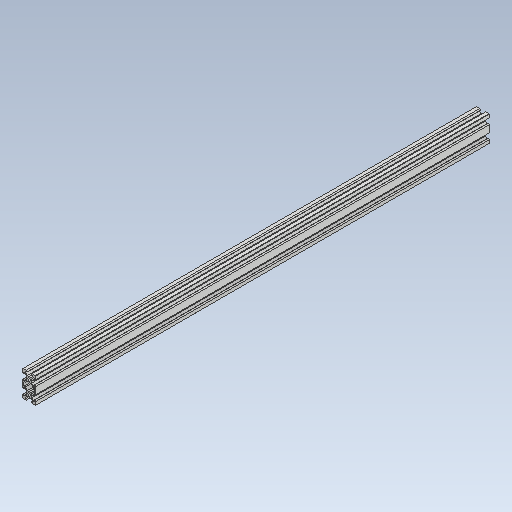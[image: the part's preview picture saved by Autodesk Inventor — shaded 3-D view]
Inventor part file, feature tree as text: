
AUTODESK INVENTOR PART (.ipt)
format: ipt  version: 2020 (Build 240168000, 168)  size: 220,160 bytes
history: native  units: mm
features: extrude x1, sketch x1
ambient origin geometry x8: Origin, YZ Plane, XZ Plane, XY Plane, X Axis, Y Axis, Z Axis, Center Point
bodies: Solid1 (feature_tree)
feature tree (2):
  extrude  "Extrusion1"  [1 undecoded]
  sketch  "Sketch1"  dims[d0=700.0mm d1=0.0mm]
note: 1 required parameter value undecoded (feature->parameter linkage not recoverable at this tier; creation-order binding heuristic only, values carry confidence <= 0.55)
